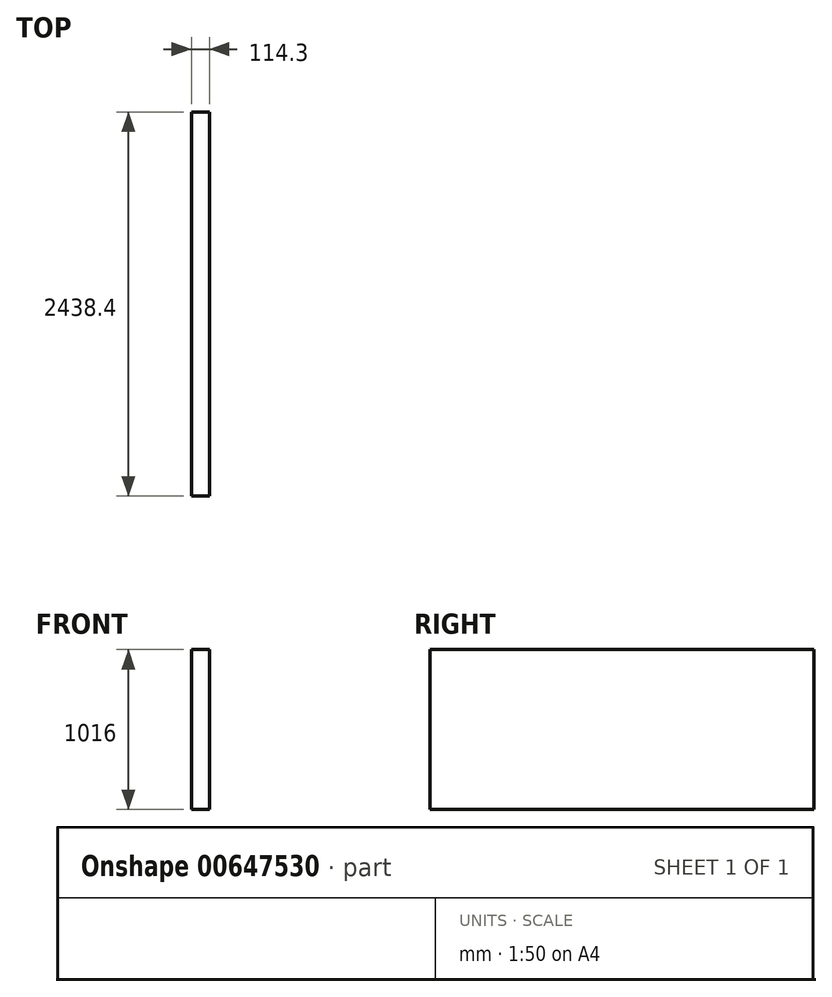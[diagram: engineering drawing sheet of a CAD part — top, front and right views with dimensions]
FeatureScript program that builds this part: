
annotation { "Feature Type Name" : "Feature", "Feature Type Description" : "" }
export const myFeature = defineFeature(function(context is Context, id is Id, definition is map)
    precondition{}
    {
        {
            var Q0;
            Q0=qCreatedBy(makeId("Front.planeOp"),FACE);
            var sketch = newSketch(context, id + "F0", { "sketchPlane" : qUnion([Q0])});
            skLineSegment(sketch, "E0.bottom", {"start": v(0, 0) * mm, "end": v(114.3, 0) * mm});
            skLineSegment(sketch, "E0.top", {"start": v(0, 1016) * mm, "end": v(114.3, 1016) * mm});
            skLineSegment(sketch, "E0.left", {"start": v(0, 0) * mm, "end": v(0, 1016) * mm});
            skLineSegment(sketch, "E0.right", {"start": v(114.3, 0) * mm, "end": v(114.3, 1016) * mm});
            skSolve(sketch);
        }
        {
            var Q0;
            Q0=makeQuery(id+"F0.imprint","IMPRINT",FACE,{"disambiguationData":[TD([[makeQuery(id+"F0.imprint","IMPRINT",EDGE,{"derivedFrom":sQuery(id+"F0.wireOp",EDGE,"E0.bottom")}),1.0]])]});
            extrude(context, id + "F1", {"entities" : qUnion([Q0]), "depth" : 2438.4 * mm, "offsetDistance" : 25.4 * mm});
        }
    });
